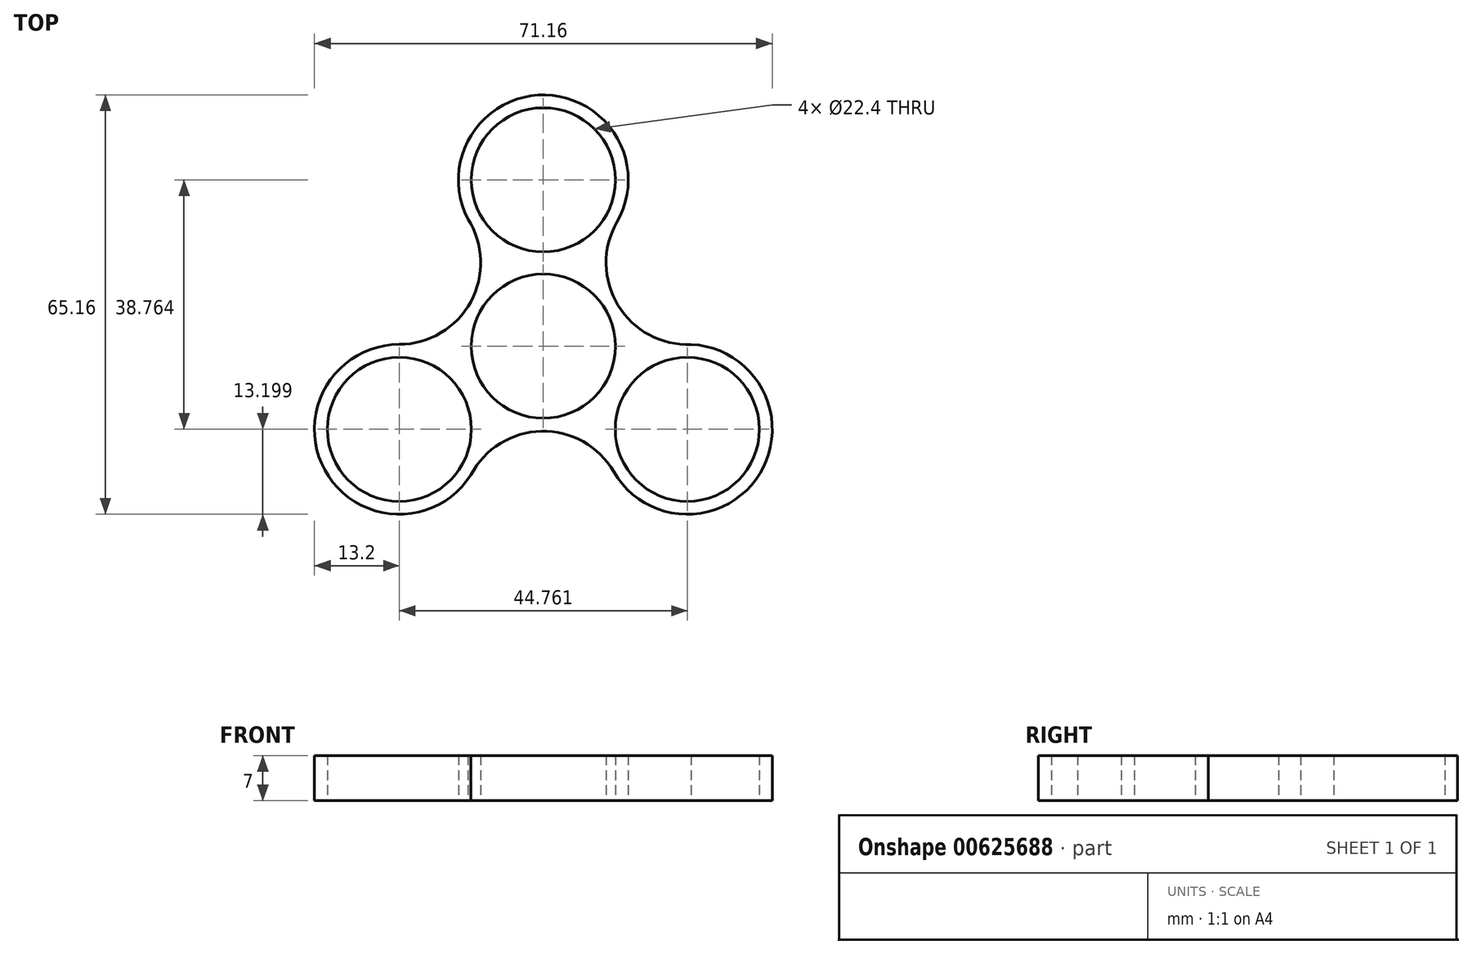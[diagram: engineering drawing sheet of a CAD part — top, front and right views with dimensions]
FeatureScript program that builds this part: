
annotation { "Feature Type Name" : "Feature", "Feature Type Description" : "" }
export const myFeature = defineFeature(function(context is Context, id is Id, definition is map)
    precondition{}
    {
        {
            var Q0;
            Q0=qCreatedBy(makeId("Top.planeOp"),FACE);
            var sketch = newSketch(context, id + "F0", { "sketchPlane" : qUnion([Q0])});
            skCircle(sketch, "E0", {"center": v(0, 0) * mm, "radius": 11.2 * mm});
            skCircle(sketch, "E1", {"center": v(0, 25.84) * mm, "radius": 11.2 * mm});
            skCircle(sketch, "E2.1.0", {"center": v(-22.38, -12.92) * mm, "radius": 11.2 * mm});
            skCircle(sketch, "E2.2.0", {"center": v(22.38, -12.92) * mm, "radius": 11.2 * mm});
            skArc(sketch, "E3", {"start": v(11.43, 19.24) * mm, "mid": v(-0.27, 39.04) * mm, "end": v(-11.15, 18.78) * mm});
            skArc(sketch, "E4.1.0", {"start": v(-22.38, 0.28) * mm, "mid": v(-33.68, -19.75) * mm, "end": v(-10.7, -19.05) * mm});
            skArc(sketch, "E4.2.0", {"start": v(10.95, -19.52) * mm, "mid": v(33.94, -19.29) * mm, "end": v(21.85, 0.27) * mm});
            skArc(sketch, "E5", {"start": v(-22.38, 0.28) * mm, "mid": v(-11.3, 6.88) * mm, "end": v(-11.72, 19.77) * mm});
            skArc(sketch, "E6.1.0", {"start": v(10.95, -19.52) * mm, "mid": v(-0.3, -13.22) * mm, "end": v(-11.26, -20.03) * mm});
            skArc(sketch, "E6.2.0", {"start": v(11.43, 19.24) * mm, "mid": v(11.6, 6.35) * mm, "end": v(22.98, 0.27) * mm});
            skSolve(sketch);
        }
        {
            var Q0;
            Q0=makeQuery(id+"F0.imprint","IMPRINT",FACE,{"disambiguationData":[TD([[makeQuery(id+"F0.imprint","IMPRINT",EDGE,{"derivedFrom":sQuery(id+"F0.wireOp",EDGE,"E0")}),-1.0]])]});
            extrude(context, id + "F1", {"entities" : qUnion([Q0]), "depth" : 7 * mm, "offsetDistance" : 25 * mm});
        }
    });
